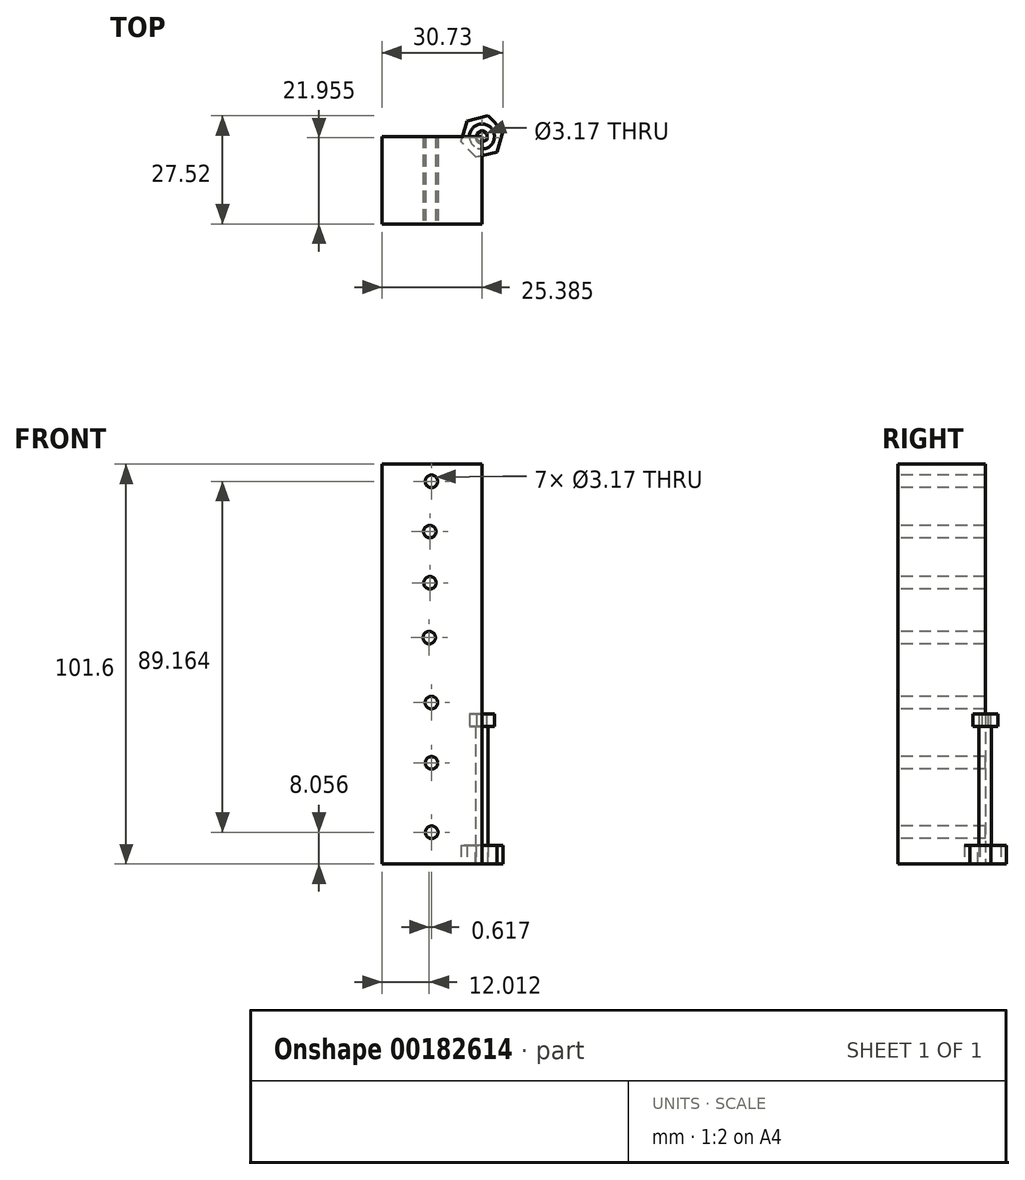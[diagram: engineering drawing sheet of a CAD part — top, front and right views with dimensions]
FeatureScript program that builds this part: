
annotation { "Feature Type Name" : "Feature", "Feature Type Description" : "" }
export const myFeature = defineFeature(function(context is Context, id is Id, definition is map)
    precondition{}
    {
        {
            var Q0;
            Q0=qCreatedBy(makeId("Top.planeOp"),FACE);
            var sketch = newSketch(context, id + "F0", { "sketchPlane" : qUnion([Q0])});
            skCircle(sketch, "E0.cCircle", {"center": v(0, 0) * mm, "radius": 4.76 * mm, "construction": true});
            skLineSegment(sketch, "E0.0", {"start": v(-1.5, -5.3) * mm, "end": v(-5.33, -1.35) * mm});
            skLineSegment(sketch, "E0.1", {"start": v(-5.33, -1.35) * mm, "end": v(-3.84, 3.94) * mm});
            skLineSegment(sketch, "E0.2", {"start": v(-3.84, 3.94) * mm, "end": v(1.5, 5.3) * mm});
            skLineSegment(sketch, "E0.3", {"start": v(1.5, 5.3) * mm, "end": v(5.33, 1.35) * mm});
            skLineSegment(sketch, "E0.4", {"start": v(5.33, 1.35) * mm, "end": v(3.84, -3.94) * mm});
            skLineSegment(sketch, "E0.5", {"start": v(3.84, -3.94) * mm, "end": v(-1.5, -5.3) * mm});
            skPoint(sketch, "E0.0.midPoint", {"position": v(-3.41, -3.32) * mm});
            skSolve(sketch);
        }
        {
            var Q0;
            Q0=makeQuery(id+"F0.imprint","IMPRINT",FACE,{"disambiguationData":[TD([[makeQuery(id+"F0.imprint","IMPRINT",EDGE,{"derivedFrom":sQuery(id+"F0.wireOp",EDGE,"E0.0")}),-1.0]])]});
            extrude(context, id + "F1", {"entities" : qUnion([Q0]), "depth" : 4.76 * mm});
        }
        {
            var Q0;
            Q0=makeQuery(id+"F1.opExtrude","CAP_FACE",FACE,{"disambiguationData":[OSD([sQuery(id+"F0.wireOp",EDGE,"E0.0"),sQuery(id+"F0.wireOp",EDGE,"E0.1"),sQuery(id+"F0.wireOp",EDGE,"E0.2"),sQuery(id+"F0.wireOp",EDGE,"E0.3"),sQuery(id+"F0.wireOp",EDGE,"E0.4"),sQuery(id+"F0.wireOp",EDGE,"E0.5")])],"isStart":false});
            var sketch = newSketch(context, id + "F2", { "sketchPlane" : qUnion([Q0])});
            skCircle(sketch, "E1", {"center": v(-0.01, -0.28) * mm, "radius": 1.59 * mm});
            skSolve(sketch);
        }
        {
            var Q0;
            Q0 = qSketchRegion(id + "F2", true);
            extrude(context, id + "F3", {"entities" : qUnion([Q0]), "operationType" : NewBodyOperationType.REMOVE, "oppositeDirection" : true, "depth" : 25.4 * mm});
        }
        {
            var Q0;
            Q0=qCreatedBy(makeId("Top.planeOp"),FACE);
            var sketch = newSketch(context, id + "F4", { "sketchPlane" : qUnion([Q0])});
            skCircle(sketch, "E2", {"center": v(0, 0) * mm, "radius": 1.59 * mm});
            skSolve(sketch);
        }
        {
            var Q0;
            Q0=makeQuery(id+"F4.imprint","IMPRINT",FACE,{"disambiguationData":[TD([[makeQuery(id+"F4.imprint","IMPRINT",EDGE,{"derivedFrom":sQuery(id+"F4.wireOp",EDGE,"E2")}),1.0]])]});
            extrude(context, id + "F5", {"entities" : qUnion([Q0]), "depth" : 34.92 * mm});
        }
        {
            var Q0;
            Q0=makeQuery(id+"F5.opExtrude","CAP_FACE",FACE,{"disambiguationData":[OSD([sQuery(id+"F4.wireOp",EDGE,"E2")])],"isStart":false});
            var sketch = newSketch(context, id + "F6", { "sketchPlane" : qUnion([Q0])});
            skCircle(sketch, "E3", {"center": v(0, 0) * mm, "radius": 3.18 * mm});
            skSolve(sketch);
        }
        {
            var Q0;
            Q0 = qSketchRegion(id + "F6", true);
            extrude(context, id + "F7", {"entities" : qUnion([Q0]), "operationType" : NewBodyOperationType.ADD, "depth" : 3.17 * mm});
        }
        {
            var Q0;
            Q0=makeQuery(id+"F7.opExtrude","CAP_FACE",FACE,{"disambiguationData":[OSD([sQuery(id+"F6.wireOp",EDGE,"E3")])],"isStart":false});
            var sketch = newSketch(context, id + "F8", { "sketchPlane" : qUnion([Q0])});
            skCircle(sketch, "E4.cCircle", {"center": v(0, 0) * mm, "radius": 1.26 * mm, "construction": true});
            skLineSegment(sketch, "E4.0", {"start": v(1.26, 0.73) * mm, "end": v(1.26, -0.73) * mm});
            skLineSegment(sketch, "E4.1", {"start": v(1.26, -0.73) * mm, "end": v(0, -1.45) * mm});
            skLineSegment(sketch, "E4.2", {"start": v(0, -1.45) * mm, "end": v(-1.26, -0.73) * mm});
            skLineSegment(sketch, "E4.3", {"start": v(-1.26, -0.73) * mm, "end": v(-1.26, 0.73) * mm});
            skLineSegment(sketch, "E4.4", {"start": v(-1.26, 0.73) * mm, "end": v(0, 1.45) * mm});
            skLineSegment(sketch, "E4.5", {"start": v(0, 1.45) * mm, "end": v(1.26, 0.73) * mm});
            skPoint(sketch, "E4.0.midPoint", {"position": v(1.26, 0) * mm});
            skSolve(sketch);
        }
        {
            var Q0;
            Q0=makeQuery(id+"F8.imprint","IMPRINT",FACE,{"disambiguationData":[TD([[makeQuery(id+"F8.imprint","IMPRINT",EDGE,{"derivedFrom":sQuery(id+"F8.wireOp",EDGE,"E4.0")}),-1.0]])]});
            extrude(context, id + "F9", {"entities" : qUnion([Q0]), "operationType" : NewBodyOperationType.REMOVE, "oppositeDirection" : true, "depth" : 3.17 * mm});
        }
        {
            var Q0;
            Q0=qCreatedBy(makeId("Top.planeOp"),FACE);
            var sketch = newSketch(context, id + "F10", { "sketchPlane" : qUnion([Q0])});
            skLineSegment(sketch, "E5.bottom", {"start": v(0, 0) * mm, "end": v(-25.4, 0) * mm});
            skLineSegment(sketch, "E5.top", {"start": v(0, -22.23) * mm, "end": v(-25.4, -22.23) * mm});
            skLineSegment(sketch, "E5.left", {"start": v(0, 0) * mm, "end": v(0, -22.23) * mm});
            skLineSegment(sketch, "E5.right", {"start": v(-25.4, 0) * mm, "end": v(-25.4, -22.23) * mm});
            skSolve(sketch);
        }
        {
            var Q0;
            Q0 = qSketchRegion(id + "F10", true);
            extrude(context, id + "F11", {"entities" : qUnion([Q0]), "depth" : 101.6 * mm});
        }
        {
            var Q0;
            Q0=makeQuery(id+"F11.opExtrude","SWEPT_FACE",FACE,{"disambiguationData":[OSD([sQuery(id+"F10.wireOp",EDGE,"E5.top")])]});
            var sketch = newSketch(context, id + "F12", { "sketchPlane" : qUnion([Q0])});
            skCircle(sketch, "E6", {"center": v(-12.77, 8.06) * mm, "radius": 1.59 * mm});
            skCircle(sketch, "E7", {"center": v(-12.85, 41) * mm, "radius": 1.59 * mm});
            skCircle(sketch, "E8", {"center": v(-12.81, 25.7) * mm, "radius": 1.59 * mm});
            skCircle(sketch, "E9", {"center": v(-13.39, 57.5) * mm, "radius": 1.59 * mm});
            skCircle(sketch, "E10", {"center": v(-13.2, 71.44) * mm, "radius": 1.59 * mm});
            skCircle(sketch, "E11", {"center": v(-13.25, 84.45) * mm, "radius": 1.59 * mm});
            skCircle(sketch, "E12", {"center": v(-12.83, 97.22) * mm, "radius": 1.59 * mm});
            skSolve(sketch);
        }
        {
            var Q0;
            Q0=makeQuery(id+"F12.imprint","IMPRINT",FACE,{"disambiguationData":[TD([[makeQuery(id+"F12.imprint","IMPRINT",EDGE,{"derivedFrom":sQuery(id+"F12.wireOp",EDGE,"E6")}),1.0]])]});
            var Q1;
            Q1=makeQuery(id+"F12.imprint","IMPRINT",FACE,{"disambiguationData":[TD([[makeQuery(id+"F12.imprint","IMPRINT",EDGE,{"derivedFrom":sQuery(id+"F12.wireOp",EDGE,"E8")}),1.0]])]});
            var Q2;
            Q2=makeQuery(id+"F12.imprint","IMPRINT",FACE,{"disambiguationData":[TD([[makeQuery(id+"F12.imprint","IMPRINT",EDGE,{"derivedFrom":sQuery(id+"F12.wireOp",EDGE,"E7")}),1.0]])]});
            var Q3;
            Q3=makeQuery(id+"F12.imprint","IMPRINT",FACE,{"disambiguationData":[TD([[makeQuery(id+"F12.imprint","IMPRINT",EDGE,{"derivedFrom":sQuery(id+"F12.wireOp",EDGE,"E9")}),1.0]])]});
            var Q4;
            Q4=makeQuery(id+"F12.imprint","IMPRINT",FACE,{"disambiguationData":[TD([[makeQuery(id+"F12.imprint","IMPRINT",EDGE,{"derivedFrom":sQuery(id+"F12.wireOp",EDGE,"E10")}),1.0]])]});
            var Q5;
            Q5=makeQuery(id+"F12.imprint","IMPRINT",FACE,{"disambiguationData":[TD([[makeQuery(id+"F12.imprint","IMPRINT",EDGE,{"derivedFrom":sQuery(id+"F12.wireOp",EDGE,"E11")}),1.0]])]});
            var Q6;
            Q6=makeQuery(id+"F12.imprint","IMPRINT",FACE,{"disambiguationData":[TD([[makeQuery(id+"F12.imprint","IMPRINT",EDGE,{"derivedFrom":sQuery(id+"F12.wireOp",EDGE,"E12")}),1.0]])]});
            extrude(context, id + "F13", {"entities" : qUnion([Q0, Q1, Q2, Q3, Q4, Q5, Q6]), "operationType" : NewBodyOperationType.REMOVE, "oppositeDirection" : true, "depth" : 25.4 * mm});
        }
    });
